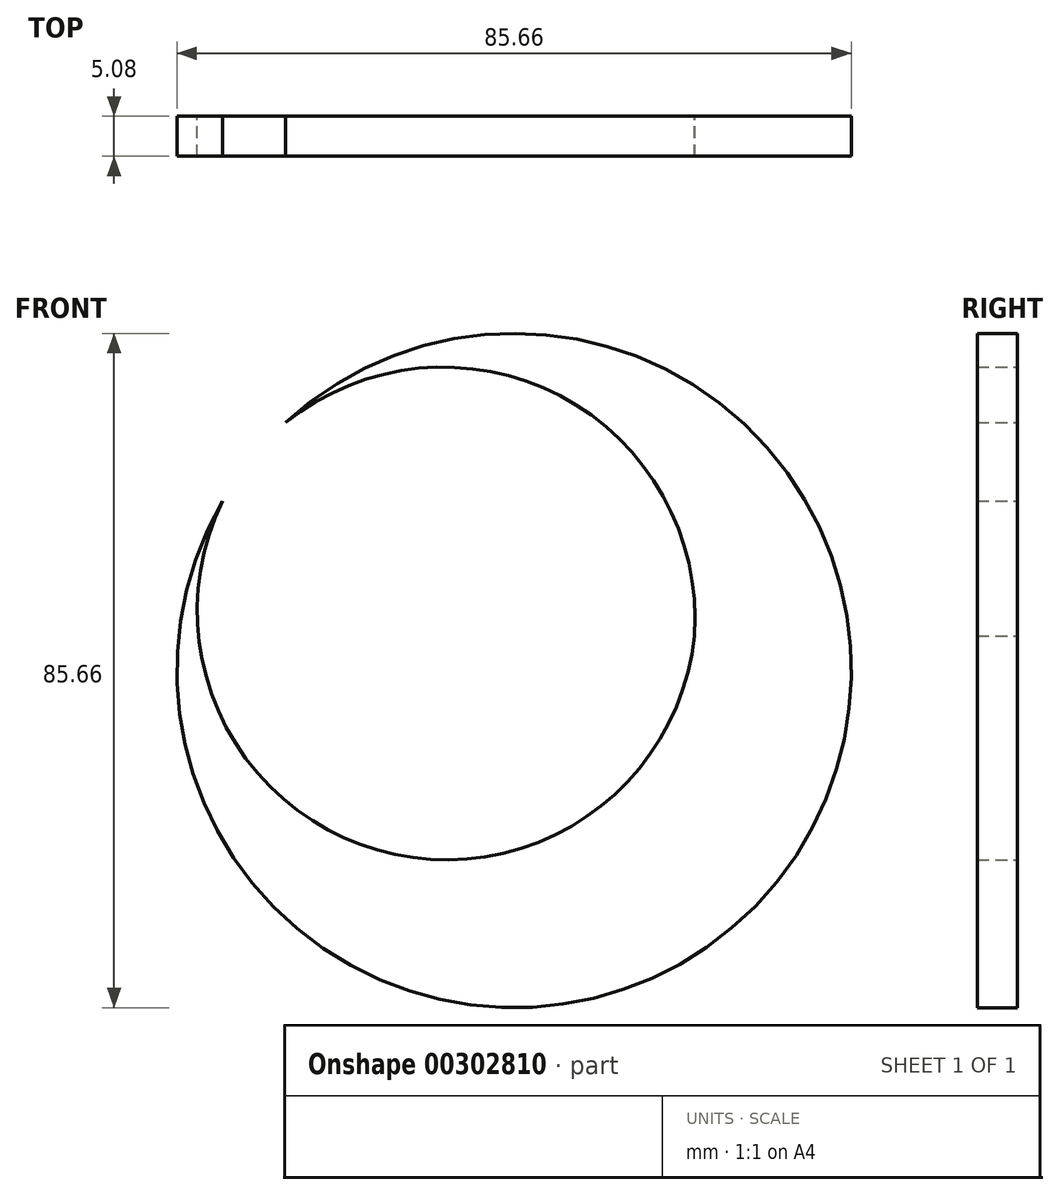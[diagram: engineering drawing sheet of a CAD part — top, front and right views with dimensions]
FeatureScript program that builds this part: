
annotation { "Feature Type Name" : "Feature", "Feature Type Description" : "" }
export const myFeature = defineFeature(function(context is Context, id is Id, definition is map)
    precondition{}
    {
        {
            var Q0;
            Q0=qCreatedBy(makeId("Front.planeOp"),FACE);
            var sketch = newSketch(context, id + "F0", { "sketchPlane" : qUnion([Q0])});
            skArc(sketch, "E0", {"start": v(-33.17, 17.2) * mm, "mid": v(37.23, -31.18) * mm, "end": v(-25.17, 27.14) * mm});
            skArc(sketch, "E1", {"start": v(26.75, 0) * mm, "mid": v(9.66, 30.55) * mm, "end": v(-25.17, 27.14) * mm});
            skArc(sketch, "E2", {"start": v(-33.17, 17.2) * mm, "mid": v(-13.47, -27.17) * mm, "end": v(26.75, 0) * mm});
            skSolve(sketch);
        }
        {
            var Q0;
            Q0 = qSketchRegion(id + "F0", true);
            extrude(context, id + "F1", {"entities" : qUnion([Q0]), "depth" : 5.08 * mm});
        }
    });
